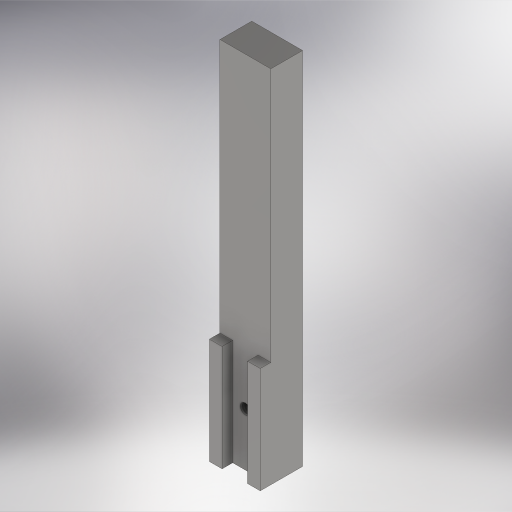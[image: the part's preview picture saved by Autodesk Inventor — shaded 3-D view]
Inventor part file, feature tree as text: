
AUTODESK INVENTOR PART (.ipt)
format: ipt  version: 2023 (Build 270158000, 158)  size: 588,800 bytes
history: native  units: mm
features: sketch x3, extrude x2, other x1, hole x1
ambient origin geometry x8: Origin, YZ Plane, XZ Plane, XY Plane, X Axis, Y Axis, Z Axis, Center Point
bodies: Body1 (feature_tree)
feature tree (7):
  other  "Sólido1"
  extrude  "Extrusão1"  Depth=15.0mm
  extrude  "Extrusão2"  Depth=12.0mm
  hole  "Furo1"  [1 undecoded]
  sketch  "Esboço1"  dims[d0=24.0mm d1=15.0mm]
  sketch  "Esboço2"  dims[d2=170.0mm d3=0.0mm d4=12.0mm]
  sketch  "Esboço3"  dims[d5=50.0mm d6=5.0mm d7=0.0mm d8=24.0mm d9=12.0mm d10=25.0mm d11=4.917mm d12=12.0mm d13=4.0mm d14=2.0mm d15=90.0deg d16=0.5mm d17=20.594885mm]
note: 1 required parameter value undecoded (feature->parameter linkage not recoverable at this tier; creation-order binding heuristic only, values carry confidence <= 0.55)
